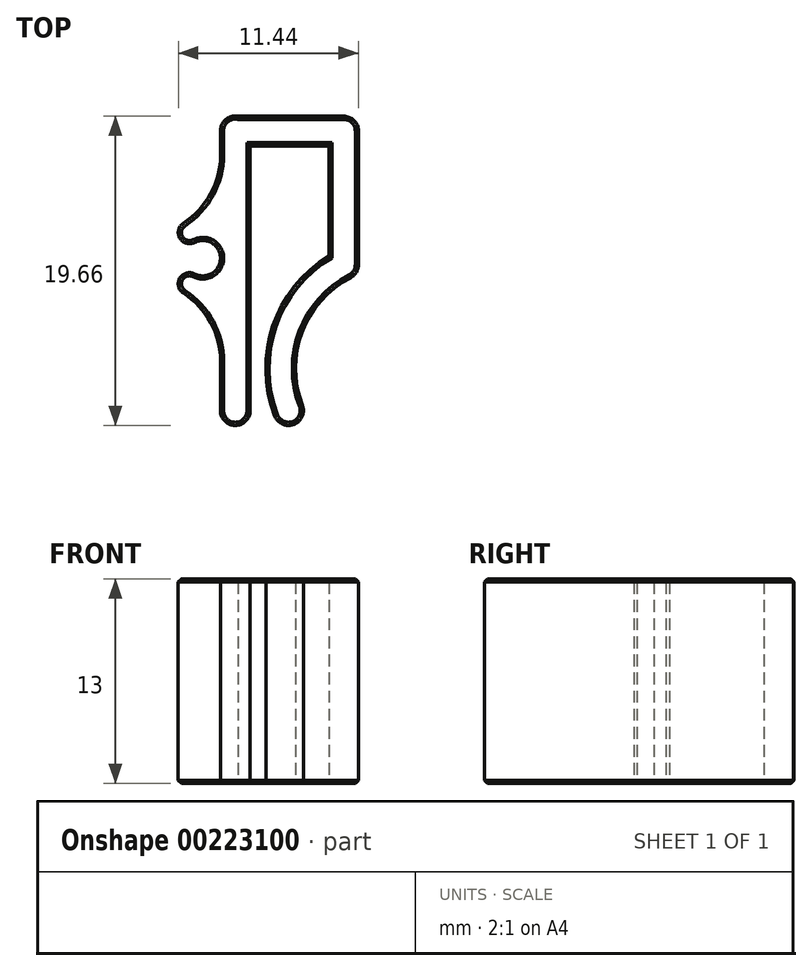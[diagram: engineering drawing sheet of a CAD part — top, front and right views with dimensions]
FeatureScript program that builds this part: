
annotation { "Feature Type Name" : "Feature", "Feature Type Description" : "" }
export const myFeature = defineFeature(function(context is Context, id is Id, definition is map)
    precondition{}
    {
        {
            var Q0;
            Q0=qCreatedBy(makeId("Top.planeOp"),FACE);
            var sketch = newSketch(context, id + "F0", { "sketchPlane" : qUnion([Q0])});
            skLineSegment(sketch, "E0", {"start": v(0, 0) * mm, "end": v(0, -33.21) * mm, "construction": true});
            skLineSegment(sketch, "E1", {"start": v(0, -33.21) * mm, "end": v(1, -33.21) * mm, "construction": true});
            skLineSegment(sketch, "E2", {"start": v(1, -33.21) * mm, "end": v(1, -7) * mm, "construction": true});
            skLineSegment(sketch, "E3", {"start": v(1, -7) * mm, "end": v(5, -7) * mm, "construction": true});
            skLineSegment(sketch, "E4", {"start": v(5, -7) * mm, "end": v(5, 0) * mm, "construction": true});
            skLineSegment(sketch, "E5", {"start": v(0, -16.82) * mm, "end": v(0, 0) * mm});
            skLineSegment(sketch, "E6.2", {"start": v(-1.88, -16.82) * mm, "end": v(-1.88, -13.7) * mm});
            skArc(sketch, "E7", {"start": v(-1.88, -16.82) * mm, "mid": v(-0.94, -17.76) * mm, "end": v(0, -16.82) * mm});
            skArc(sketch, "E8", {"start": v(-4.24, -4.91) * mm, "mid": v(-2.5, -3.04) * mm, "end": v(-1.88, -0.57) * mm});
            skArc(sketch, "E9", {"start": v(-1.88, -13.7) * mm, "mid": v(-2.5, -11.23) * mm, "end": v(-4.24, -9.36) * mm});
            skLineSegment(sketch, "E10", {"start": v(-3, -3.8) * mm, "end": v(-3, -10.48) * mm, "construction": true});
            skArc(sketch, "E11", {"start": v(-3.52, -8.14) * mm, "mid": v(-1.88, -7.14) * mm, "end": v(-3.52, -6.14) * mm});
            skArc(sketch, "E12", {"start": v(-4.24, -4.91) * mm, "mid": v(-4.46, -5.87) * mm, "end": v(-3.52, -6.14) * mm});
            skArc(sketch, "E13", {"start": v(-4.24, -9.36) * mm, "mid": v(-4.46, -8.4) * mm, "end": v(-3.52, -8.14) * mm});
            skLineSegment(sketch, "E14", {"start": v(-3.85, -5.5) * mm, "end": v(-3.85, -8.76) * mm, "construction": true});
            skLineSegment(sketch, "E15", {"start": v(-1.88, -0.57) * mm, "end": v(-1.88, -13.7) * mm, "construction": true});
            skLineSegment(sketch, "E16", {"start": v(-0.78, 1.88) * mm, "end": v(5.94, 1.88) * mm});
            skLineSegment(sketch, "E17", {"start": v(0, 0) * mm, "end": v(5, 0) * mm});
            skLineSegment(sketch, "E18", {"start": v(-1.88, 0.95) * mm, "end": v(-1.88, -0.57) * mm});
            skLineSegment(sketch, "E19", {"start": v(5, 0) * mm, "end": v(0, 0) * mm, "construction": true});
            skLineSegment(sketch, "E20", {"start": v(6.88, 0.94) * mm, "end": v(6.88, -7.55) * mm});
            skLineSegment(sketch, "E21", {"start": v(5, 0) * mm, "end": v(5, -7) * mm});
            skArc(sketch, "E22", {"start": v(5, -7) * mm, "mid": v(1.44, -11.46) * mm, "end": v(1.57, -17.16) * mm});
            skArc(sketch, "E23", {"start": v(6.37, -8.38) * mm, "mid": v(3.3, -11.85) * mm, "end": v(3.32, -16.48) * mm});
            skArc(sketch, "E24", {"start": v(3.32, -16.48) * mm, "mid": v(2.78, -17.7) * mm, "end": v(1.57, -17.16) * mm});
            skLineSegment(sketch, "E25", {"start": v(-0.94, -16.82) * mm, "end": v(2.44, -16.82) * mm, "construction": true});
            skLineSegment(sketch, "E26", {"start": v(2.5, 0) * mm, "end": v(2.5, 1.88) * mm, "construction": true});
            skLineSegment(sketch, "E27", {"start": v(0, -12.98) * mm, "end": v(-1.88, -12.98) * mm, "construction": true});
            skLineSegment(sketch, "E28", {"start": v(5, -3.5) * mm, "end": v(6.88, -3.5) * mm, "construction": true});
            skPoint(sketch, "E29.visualSharp", {"position": v(6.88, 1.88) * mm});
            skArc(sketch, "E29.filletArc", {"start": v(6.88, 0.94) * mm, "mid": v(6.6, 1.6) * mm, "end": v(5.94, 1.88) * mm});
            skPoint(sketch, "E30.visualSharp", {"position": v(6.88, -8.15) * mm});
            skArc(sketch, "E30.filletArc", {"start": v(6.37, -8.38) * mm, "mid": v(6.74, -8.04) * mm, "end": v(6.88, -7.55) * mm});
            skArc(sketch, "E31", {"start": v(-1.88, 0.95) * mm, "mid": v(-1.55, 1.67) * mm, "end": v(-0.78, 1.88) * mm});
            skSolve(sketch);
        }
        {
            var Q0;
            Q0=makeQuery(id+"F0.imprint","IMPRINT",FACE,{"disambiguationData":[TD([[makeQuery(id+"F0.imprint","IMPRINT",EDGE,{"derivedFrom":sQuery(id+"F0.wireOp",EDGE,"E5")}),1.0]])]});
            extrude(context, id + "F1", {"entities" : qUnion([Q0]), "depth" : 13 * mm});
        }
        {
            var Q0;
            Q0=makeQuery(id+"F1.opExtrude","CAP_FACE",FACE,{"disambiguationData":[OSD([sQuery(id+"F0.wireOp",EDGE,"E5"),sQuery(id+"F0.wireOp",EDGE,"E6.2"),sQuery(id+"F0.wireOp",EDGE,"E7"),sQuery(id+"F0.wireOp",EDGE,"E8"),sQuery(id+"F0.wireOp",EDGE,"E9"),sQuery(id+"F0.wireOp",EDGE,"E11"),sQuery(id+"F0.wireOp",EDGE,"E12"),sQuery(id+"F0.wireOp",EDGE,"E13"),sQuery(id+"F0.wireOp",EDGE,"E16"),sQuery(id+"F0.wireOp",EDGE,"E17"),sQuery(id+"F0.wireOp",EDGE,"E18"),sQuery(id+"F0.wireOp",EDGE,"E20"),sQuery(id+"F0.wireOp",EDGE,"E21"),sQuery(id+"F0.wireOp",EDGE,"E22"),sQuery(id+"F0.wireOp",EDGE,"E23"),sQuery(id+"F0.wireOp",EDGE,"E24"),sQuery(id+"F0.wireOp",EDGE,"E29.filletArc"),sQuery(id+"F0.wireOp",EDGE,"E30.filletArc"),sQuery(id+"F0.wireOp",EDGE,"E31")])],"isStart":true});
            var Q1;
            Q1=makeQuery(id+"F1.opExtrude","CAP_FACE",FACE,{"disambiguationData":[OSD([sQuery(id+"F0.wireOp",EDGE,"E5"),sQuery(id+"F0.wireOp",EDGE,"E6.2"),sQuery(id+"F0.wireOp",EDGE,"E7"),sQuery(id+"F0.wireOp",EDGE,"E8"),sQuery(id+"F0.wireOp",EDGE,"E9"),sQuery(id+"F0.wireOp",EDGE,"E11"),sQuery(id+"F0.wireOp",EDGE,"E12"),sQuery(id+"F0.wireOp",EDGE,"E13"),sQuery(id+"F0.wireOp",EDGE,"E16"),sQuery(id+"F0.wireOp",EDGE,"E17"),sQuery(id+"F0.wireOp",EDGE,"E18"),sQuery(id+"F0.wireOp",EDGE,"E20"),sQuery(id+"F0.wireOp",EDGE,"E21"),sQuery(id+"F0.wireOp",EDGE,"E22"),sQuery(id+"F0.wireOp",EDGE,"E23"),sQuery(id+"F0.wireOp",EDGE,"E24"),sQuery(id+"F0.wireOp",EDGE,"E29.filletArc"),sQuery(id+"F0.wireOp",EDGE,"E30.filletArc"),sQuery(id+"F0.wireOp",EDGE,"E31")])],"isStart":false});
            chamfer(context, id + "F2", {"entities" : qUnion([Q0, Q1]), "width" : 0.2 * mm, "tangentPropagation" : true});
        }
    });
